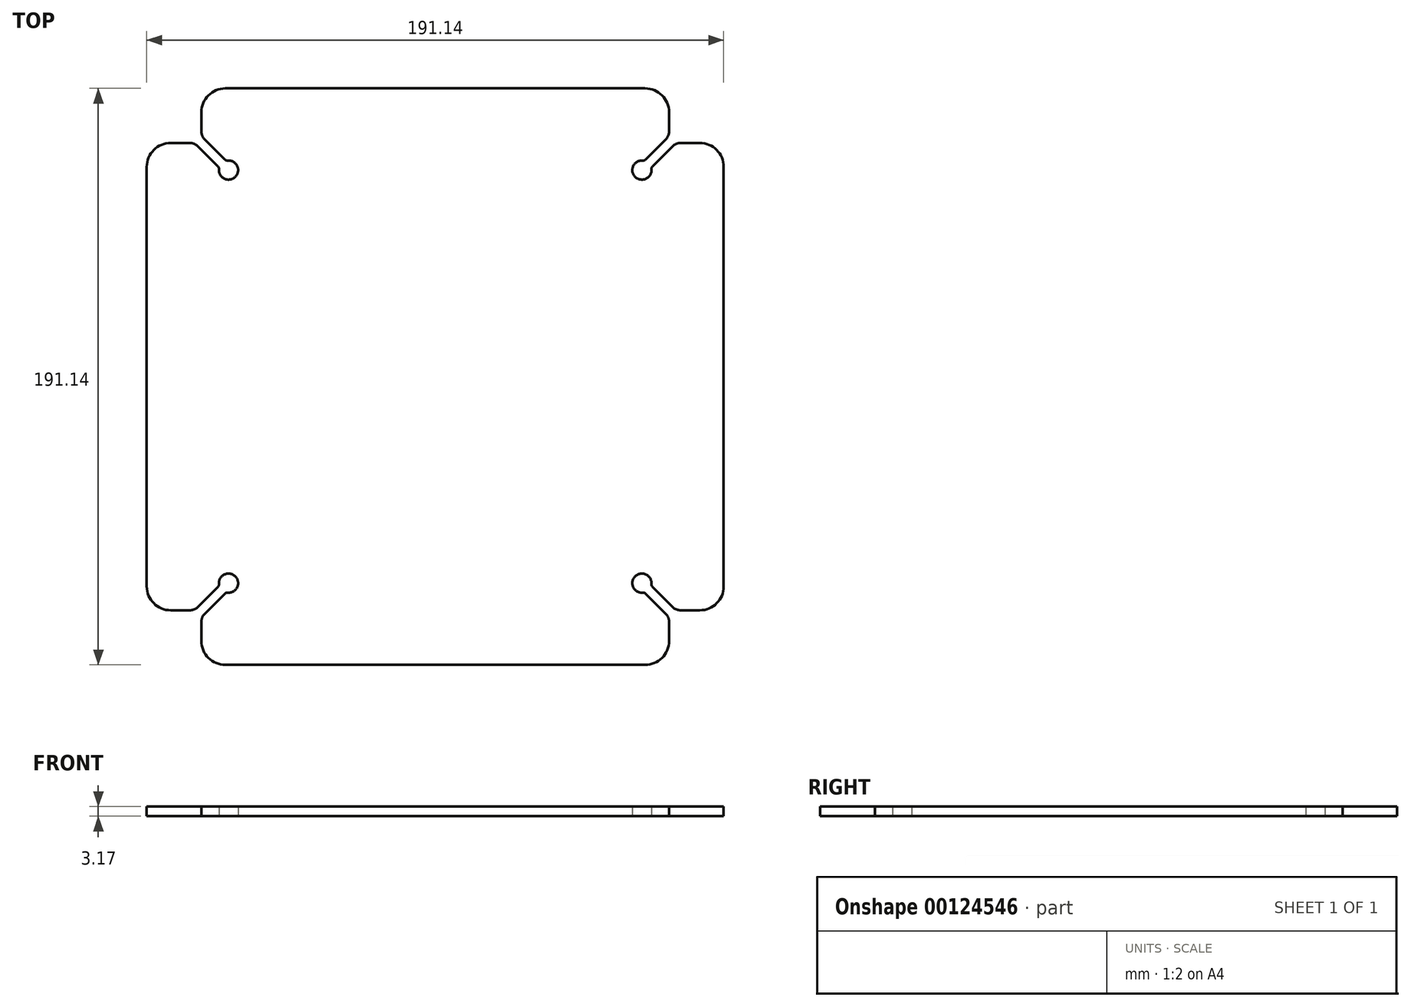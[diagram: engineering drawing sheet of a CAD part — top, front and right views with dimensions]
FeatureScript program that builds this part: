
annotation { "Feature Type Name" : "Feature", "Feature Type Description" : "" }
export const myFeature = defineFeature(function(context is Context, id is Id, definition is map)
    precondition{}
    {
        {
            var Q0;
            Q0=qCreatedBy(makeId("Top.planeOp"),FACE);
            var sketch = newSketch(context, id + "F0", { "sketchPlane" : qUnion([Q0])});
            skArc(sketch, "E0", {"start": v(95.57, 69.53) * mm, "mid": v(93.24, 75.15) * mm, "end": v(87.63, 77.47) * mm});
            skArc(sketch, "E1", {"start": v(81.3, 77.47) * mm, "mid": v(79.84, 77.18) * mm, "end": v(78.6, 76.35) * mm});
            skArc(sketch, "E2", {"start": v(68.75, 71.64) * mm, "mid": v(66.23, 66.23) * mm, "end": v(71.64, 68.75) * mm});
            skArc(sketch, "E3", {"start": v(76.35, 78.6) * mm, "mid": v(77.18, 79.84) * mm, "end": v(77.47, 81.3) * mm});
            skArc(sketch, "E4", {"start": v(77.47, 87.63) * mm, "mid": v(75.15, 93.24) * mm, "end": v(69.53, 95.57) * mm});
            skArc(sketch, "E5", {"start": v(-69.53, 95.57) * mm, "mid": v(-75.15, 93.24) * mm, "end": v(-77.47, 87.63) * mm});
            skArc(sketch, "E6", {"start": v(-77.47, 81.3) * mm, "mid": v(-77.18, 79.84) * mm, "end": v(-76.35, 78.6) * mm});
            skArc(sketch, "E7", {"start": v(-71.64, 68.75) * mm, "mid": v(-66.23, 66.23) * mm, "end": v(-68.75, 71.64) * mm});
            skArc(sketch, "E8", {"start": v(-78.6, 76.35) * mm, "mid": v(-79.84, 77.18) * mm, "end": v(-81.3, 77.47) * mm});
            skArc(sketch, "E9", {"start": v(-87.63, 77.47) * mm, "mid": v(-93.24, 75.15) * mm, "end": v(-95.57, 69.53) * mm});
            skLineSegment(sketch, "E10", {"start": v(-95.57, 69.53) * mm, "end": v(-95.57, 0) * mm});
            skLineSegment(sketch, "E11", {"start": v(95.57, 0) * mm, "end": v(95.57, 69.53) * mm});
            skLineSegment(sketch, "E12", {"start": v(87.63, 77.47) * mm, "end": v(81.3, 77.47) * mm});
            skLineSegment(sketch, "E13", {"start": v(77.47, 81.3) * mm, "end": v(77.47, 87.63) * mm});
            skLineSegment(sketch, "E14", {"start": v(69.53, 95.57) * mm, "end": v(-69.53, 95.57) * mm});
            skLineSegment(sketch, "E15", {"start": v(-77.47, 87.63) * mm, "end": v(-77.47, 81.3) * mm});
            skLineSegment(sketch, "E16", {"start": v(-81.3, 77.47) * mm, "end": v(-87.63, 77.47) * mm});
            skLineSegment(sketch, "E17", {"start": v(-95.57, 0) * mm, "end": v(0, 0) * mm, "construction": true});
            skLineSegment(sketch, "E18", {"start": v(0, 95.57) * mm, "end": v(0, 0) * mm, "construction": true});
            skLineSegment(sketch, "E19", {"start": v(-78.6, 76.35) * mm, "end": v(-72, 69.76) * mm});
            skLineSegment(sketch, "E20", {"start": v(-69.76, 72) * mm, "end": v(-76.35, 78.6) * mm});
            skLineSegment(sketch, "E21", {"start": v(0, 0) * mm, "end": v(-68.47, 68.47) * mm, "construction": true});
            skPoint(sketch, "E22.visualSharp", {"position": v(-69.3, 71.54) * mm});
            skArc(sketch, "E22.filletArc", {"start": v(-69.76, 72) * mm, "mid": v(-69.3, 71.7) * mm, "end": v(-68.75, 71.64) * mm});
            skPoint(sketch, "E23.visualSharp", {"position": v(-71.54, 69.3) * mm});
            skArc(sketch, "E23.filletArc", {"start": v(-71.64, 68.75) * mm, "mid": v(-71.7, 69.3) * mm, "end": v(-72, 69.76) * mm});
            skLineSegment(sketch, "E24", {"start": v(-77.47, 87.63) * mm, "end": v(0, 87.63) * mm, "construction": true});
            skLineSegment(sketch, "E25", {"start": v(-87.63, 77.47) * mm, "end": v(-87.63, 0) * mm, "construction": true});
            skLineSegment(sketch, "E26", {"start": v(0, 0) * mm, "end": v(68.47, 68.47) * mm, "construction": true});
            skLineSegment(sketch, "E27", {"start": v(-78.6, 76.35) * mm, "end": v(-76.35, 78.6) * mm, "construction": true});
            skLineSegment(sketch, "E28", {"start": v(69.76, 72) * mm, "end": v(76.35, 78.6) * mm});
            skLineSegment(sketch, "E29", {"start": v(78.6, 76.35) * mm, "end": v(72, 69.76) * mm});
            skLineSegment(sketch, "E30", {"start": v(76.35, 78.6) * mm, "end": v(78.6, 76.35) * mm, "construction": true});
            skPoint(sketch, "E31.visualSharp", {"position": v(69.3, 71.54) * mm});
            skArc(sketch, "E31.filletArc", {"start": v(68.75, 71.64) * mm, "mid": v(69.3, 71.7) * mm, "end": v(69.76, 72) * mm});
            skPoint(sketch, "E32.visualSharp", {"position": v(71.54, 69.3) * mm});
            skArc(sketch, "E32.filletArc", {"start": v(72, 69.76) * mm, "mid": v(71.7, 69.3) * mm, "end": v(71.64, 68.75) * mm});
            skLineSegment(sketch, "E33", {"start": v(-95.57, 0) * mm, "end": v(95.57, 0) * mm});
            skSolve(sketch);
        }
        {
            var Q0;
            Q0 = qSketchRegion(id + "F0", true);
            extrude(context, id + "F1", {"entities" : qUnion([Q0]), "depth" : 3.17 * mm});
        }
        {
            var Q0;
            Q0=makeQuery(id+"F1.opExtrude","SWEPT_BODY",BODY,{"disambiguationData":[OSD([sQuery(id+"F0.wireOp",EDGE,"E0"),sQuery(id+"F0.wireOp",EDGE,"E1"),sQuery(id+"F0.wireOp",EDGE,"E2"),sQuery(id+"F0.wireOp",EDGE,"E3"),sQuery(id+"F0.wireOp",EDGE,"E4"),sQuery(id+"F0.wireOp",EDGE,"E5"),sQuery(id+"F0.wireOp",EDGE,"E6"),sQuery(id+"F0.wireOp",EDGE,"E7"),sQuery(id+"F0.wireOp",EDGE,"E8"),sQuery(id+"F0.wireOp",EDGE,"E9"),sQuery(id+"F0.wireOp",EDGE,"E10"),sQuery(id+"F0.wireOp",EDGE,"E11"),sQuery(id+"F0.wireOp",EDGE,"E12"),sQuery(id+"F0.wireOp",EDGE,"E13"),sQuery(id+"F0.wireOp",EDGE,"E14"),sQuery(id+"F0.wireOp",EDGE,"E15"),sQuery(id+"F0.wireOp",EDGE,"E16"),sQuery(id+"F0.wireOp",EDGE,"E19"),sQuery(id+"F0.wireOp",EDGE,"E20"),sQuery(id+"F0.wireOp",EDGE,"E22.filletArc"),sQuery(id+"F0.wireOp",EDGE,"E23.filletArc"),sQuery(id+"F0.wireOp",EDGE,"E28"),sQuery(id+"F0.wireOp",EDGE,"E29"),sQuery(id+"F0.wireOp",EDGE,"E31.filletArc"),sQuery(id+"F0.wireOp",EDGE,"E32.filletArc"),sQuery(id+"F0.wireOp",EDGE,"E33")])]});
            var Q1;
            Q1=qCreatedBy(makeId("Front.planeOp"),FACE);
            mirror(context, id + "F2", {"operationType" : NewBodyOperationType.ADD, "entities" : qUnion([Q0]), "mirrorPlane" : qUnion([Q1])});
        }
    });
